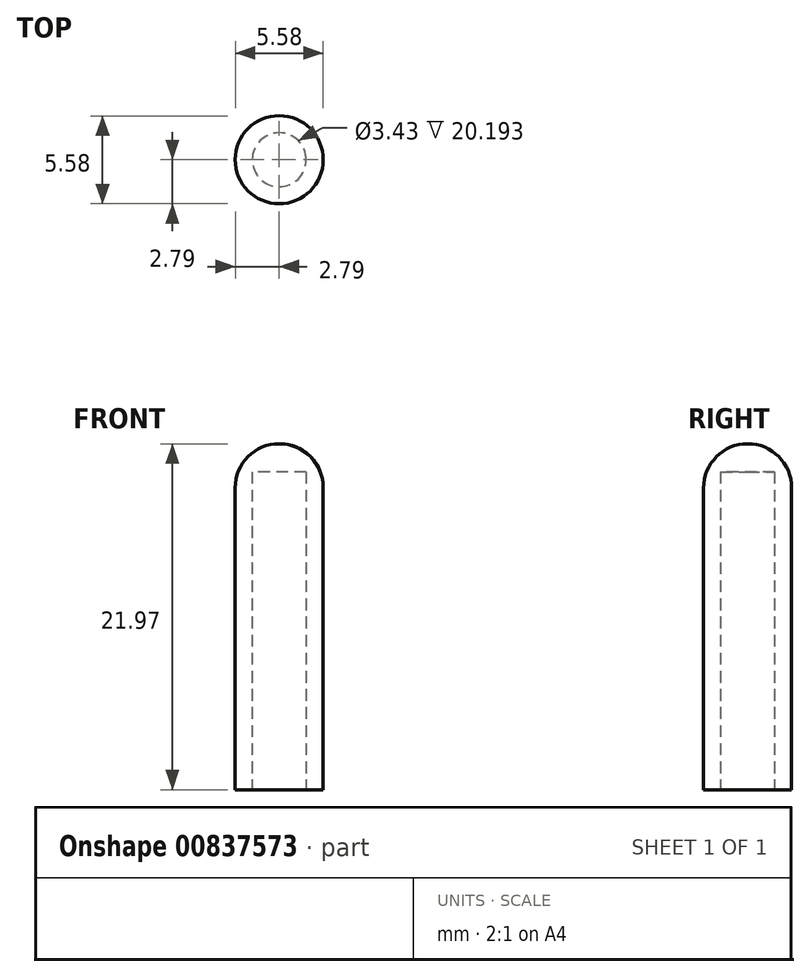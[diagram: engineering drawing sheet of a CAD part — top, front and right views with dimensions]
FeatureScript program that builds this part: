
annotation { "Feature Type Name" : "Feature", "Feature Type Description" : "" }
export const myFeature = defineFeature(function(context is Context, id is Id, definition is map)
    precondition{}
    {
        {
            var Q0;
            Q0=qCreatedBy(makeId("Top.planeOp"),FACE);
            var sketch = newSketch(context, id + "F0", { "sketchPlane" : qUnion([Q0])});
            skCircle(sketch, "E0", {"center": v(0, 0) * mm, "radius": 2.8 * mm});
            skCircle(sketch, "E1", {"center": v(0, 0) * mm, "radius": 1.71 * mm});
            skSolve(sketch);
        }
        {
            var Q0;
            Q0 = qSketchRegion(id + "F0", true);
            extrude(context, id + "F1", {"entities" : qUnion([Q0]), "depth" : 21.97 * mm, "offsetDistance" : 25.4 * mm});
        }
        {
            var Q0;
            Q0=makeQuery(id+"F1.opExtrude","CAP_FACE",FACE,{"disambiguationData":[OSD([sQuery(id+"F0.wireOp",EDGE,"E0"),sQuery(id+"F0.wireOp",EDGE,"E1")])],"isStart":false});
            var sketch = newSketch(context, id + "F2", { "sketchPlane" : qUnion([Q0])});
            skCircle(sketch, "E2", {"center": v(0, 0) * mm, "radius": 1.71 * mm});
            skSolve(sketch);
        }
        {
            var Q0;
            Q0 = qSketchRegion(id + "F2", true);
            extrude(context, id + "F3", {"entities" : qUnion([Q0]), "operationType" : NewBodyOperationType.ADD, "oppositeDirection" : true, "depth" : 1.78 * mm, "offsetDistance" : 25.4 * mm});
        }
        {
            var Q0;
            Q0=makeQuery(id+"F3.boolean.opBoolean","MERGE",FACE,{"derivedFrom":[makeQuery(id+"F1.opExtrude","CAP_FACE",FACE,{"disambiguationData":[OSD([sQuery(id+"F0.wireOp",EDGE,"E0"),sQuery(id+"F0.wireOp",EDGE,"E1")])],"isStart":false}),makeQuery(id+"F3.opExtrude","CAP_FACE",FACE,{"disambiguationData":[OSD([sQuery(id+"F2.wireOp",EDGE,"E2")])],"isStart":true})]});
            fillet(context, id + "F4", {"entities" : qUnion([Q0]), "radius" : 2.8 * mm, "tangentPropagation" : true, "allowEdgeOverflow" : false});
        }
    });
